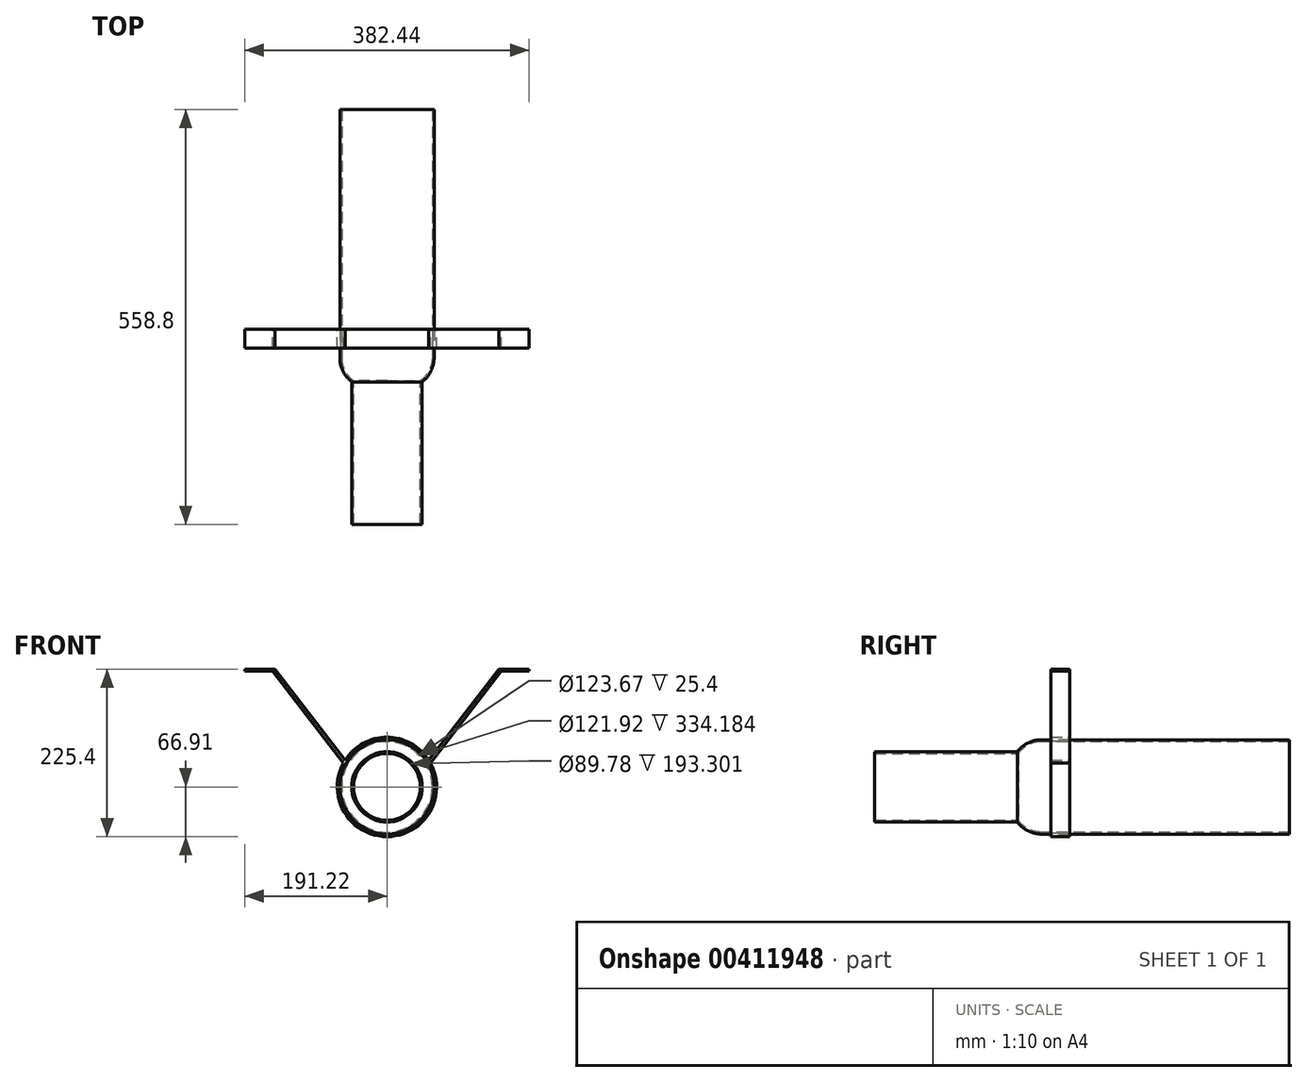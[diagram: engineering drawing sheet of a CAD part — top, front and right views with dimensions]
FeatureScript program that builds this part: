
annotation { "Feature Type Name" : "Feature", "Feature Type Description" : "" }
export const myFeature = defineFeature(function(context is Context, id is Id, definition is map)
    precondition{}
    {
        {
            var Q0;
            Q0=qCreatedBy(makeId("Front.planeOp"),FACE);
            var sketch = newSketch(context, id + "F0", { "sketchPlane" : qUnion([Q0])});
            skCircle(sketch, "E0", {"center": v(0, 0) * mm, "radius": 63.5 * mm});
            skSolve(sketch);
        }
        {
            var Q0;
            Q0 = qSketchRegion(id + "F0", true);
            extrude(context, id + "F1", {"entities" : qUnion([Q0]), "oppositeDirection" : true, "depth" : 366.78 * mm});
        }
        {
            var Q0;
            Q0=makeQuery(id+"F1.opExtrude","CAP_FACE",FACE,{"disambiguationData":[OSD([sQuery(id+"F0.wireOp",EDGE,"E0")])],"isStart":true});
            var sketch = newSketch(context, id + "F2", { "sketchPlane" : qUnion([Q0])});
            skCircle(sketch, "E1", {"center": v(0, 0) * mm, "radius": 47.43 * mm});
            skSolve(sketch);
        }
        {
            var Q0;
            Q0 = qSketchRegion(id + "F2", true);
            extrude(context, id + "F3", {"entities" : qUnion([Q0]), "operationType" : NewBodyOperationType.ADD, "depth" : 192.02 * mm});
        }
        {
            var Q0;
            Q0=makeQuery(id+"F1.opExtrude","CAP_EDGE",EDGE,{"disambiguationData":[OSD([sQuery(id+"F0.wireOp",EDGE,"E0")])],"isStart":true});
            fillet(context, id + "F4", {"entities" : qUnion([Q0]), "radius" : 41.1 * mm, "tangentPropagation" : true, "allowEdgeOverflow" : false});
        }
        {
            var Q0;
            Q0=makeQuery(id+"F3.opExtrude","CAP_FACE",FACE,{"disambiguationData":[OSD([sQuery(id+"F2.wireOp",EDGE,"E1")])],"isStart":false});
            var Q1;
            Q1=makeQuery(id+"F1.opExtrude","CAP_FACE",FACE,{"disambiguationData":[OSD([sQuery(id+"F0.wireOp",EDGE,"E0")])],"isStart":false});
            shell(context, id + "F5", {"entities" : qUnion([Q0, Q1]), "thickness" : 2.54 * mm});
        }
        {
            var Q0;
            Q0=qCreatedBy(makeId("Front.planeOp"),FACE);
            cPlane(context, id + "F6", {"entities" : qUnion([Q0]), "cplaneType" : CPlaneType.OFFSET, "offset" : 70.61 * mm, "oppositeDirection" : true, "width" : 152.4 * mm, "height" : 152.4 * mm});
        }
        {
            var Q0;
            Q0=qCreatedBy(id+"F6.planeOp",FACE);
            var sketch = newSketch(context, id + "F7", { "sketchPlane" : qUnion([Q0])});
            skCircle(sketch, "E2", {"center": v(0, 0) * mm, "radius": 66.91 * mm});
            skSolve(sketch);
        }
        {
            var Q0;
            Q0 = qSketchRegion(id + "F7", true);
            extrude(context, id + "F8", {"entities" : qUnion([Q0]), "depth" : 25.4 * mm});
        }
        {
            var Q0;
            Q0=makeQuery(id+"F8.opExtrude","CAP_FACE",FACE,{"disambiguationData":[OSD([sQuery(id+"F7.wireOp",EDGE,"E2")])],"isStart":false});
            shell(context, id + "F9", {"entities" : qUnion([Q0]), "thickness" : 5.08 * mm});
        }
        {
            var Q0;
            Q0=qCreatedBy(id+"F6.planeOp",FACE);
            var sketch = newSketch(context, id + "F10", { "sketchPlane" : qUnion([Q0])});
            skLineSegment(sketch, "E3", {"start": v(-58.56, 32.15) * mm, "end": v(-154.19, 155.85) * mm});
            skLineSegment(sketch, "E4.0", {"start": v(-55.15, 34.79) * mm, "end": v(-150.77, 158.5) * mm});
            skLineSegment(sketch, "E5", {"start": v(-154.19, 155.85) * mm, "end": v(-191.22, 155.85) * mm});
            skLineSegment(sketch, "E6", {"start": v(-191.22, 155.85) * mm, "end": v(-191.22, 158.5) * mm});
            skLineSegment(sketch, "E7", {"start": v(-191.22, 158.5) * mm, "end": v(-150.77, 158.5) * mm});
            skLineSegment(sketch, "E8", {"start": v(-55.15, 34.79) * mm, "end": v(-58.56, 32.15) * mm});
            skLineSegment(sketch, "E9", {"start": v(0, 172.13) * mm, "end": v(0, -144.05) * mm, "construction": true});
            skLineSegment(sketch, "E10.MirrorCS", {"start": v(191.22, 158.5) * mm, "end": v(150.77, 158.5) * mm});
            skLineSegment(sketch, "E11.MirrorCS", {"start": v(55.15, 34.79) * mm, "end": v(150.77, 158.5) * mm});
            skLineSegment(sketch, "E12.MirrorCS", {"start": v(55.15, 34.79) * mm, "end": v(58.56, 32.15) * mm});
            skLineSegment(sketch, "E13.MirrorCS", {"start": v(58.56, 32.15) * mm, "end": v(154.19, 155.85) * mm});
            skLineSegment(sketch, "E14.MirrorCS", {"start": v(154.19, 155.85) * mm, "end": v(191.22, 155.85) * mm});
            skLineSegment(sketch, "E15.MirrorCS", {"start": v(191.22, 155.85) * mm, "end": v(191.22, 158.5) * mm});
            skSolve(sketch);
        }
        {
            var Q0;
            Q0 = qSketchRegion(id + "F10", true);
            extrude(context, id + "F11", {"entities" : qUnion([Q0]), "operationType" : NewBodyOperationType.ADD, "depth" : 25.4 * mm});
        }
        {
            var Q0;
            {var subQ0=sQuery(id+"F7.wireOp",EDGE,"E2");Q0=makeQuery(id+"F9.opShell","OFFSET_FACE",FACE,{"disambiguationData":[OSD([subQ0]),TDD([makeQuery(id+"F8.opExtrude","CAP_FACE",FACE,{"disambiguationData":[OSD([subQ0])],"isStart":true})])]});}
            var Q1;
            Q1=makeQuery(id+"F11.boolean.opBoolean","MERGE",FACE,{"derivedFrom":[makeQuery(id+"F8.opExtrude","CAP_FACE",FACE,{"disambiguationData":[OSD([sQuery(id+"F7.wireOp",EDGE,"E2")])],"isStart":true}),makeQuery(id+"F11.opExtrude","CAP_FACE",FACE,{"disambiguationData":[OSD([sQuery(id+"F10.wireOp",EDGE,"E3"),sQuery(id+"F10.wireOp",EDGE,"E4.0"),sQuery(id+"F10.wireOp",EDGE,"E5"),sQuery(id+"F10.wireOp",EDGE,"E6"),sQuery(id+"F10.wireOp",EDGE,"E7"),sQuery(id+"F10.wireOp",EDGE,"E8")])],"isStart":true}),makeQuery(id+"F11.opExtrude","CAP_FACE",FACE,{"disambiguationData":[OSD([sQuery(id+"F10.wireOp",EDGE,"E10.MirrorCS"),sQuery(id+"F10.wireOp",EDGE,"E11.MirrorCS"),sQuery(id+"F10.wireOp",EDGE,"E12.MirrorCS"),sQuery(id+"F10.wireOp",EDGE,"E13.MirrorCS"),sQuery(id+"F10.wireOp",EDGE,"E14.MirrorCS"),sQuery(id+"F10.wireOp",EDGE,"E15.MirrorCS")])],"isStart":true})]});
            shell(context, id + "F12", {"entities" : qUnion([Q0, Q1]), "thickness" : 5.08 * mm});
        }
    });
